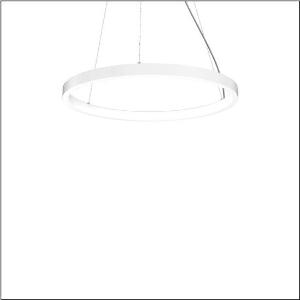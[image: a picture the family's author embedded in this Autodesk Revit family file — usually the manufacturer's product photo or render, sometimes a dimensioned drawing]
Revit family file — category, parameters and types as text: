
# Revit family: silica_r__21_ring-i_5pjbi3d1004a_d7a1
name_source: partatom
category: Lighting Fixtures
units: mm (PartAtom-declared; Revit-internal decimal feet)

## family parameters
Cut with Voids When Loaded = No
Host = Face
Light Source = No
Part Type = Normal
Room Calculation Point = No
Round Connector Dimension = Use Diameter
Shared = No

## types (1)
- Silica® 21 Ring-I (1 x LED, 6120 lm, 105 W, 3000K)
    Apparent Load = 105 VA
    CIE Flux Codes = 22 48 76 50 101
    Color Rendering = 80
    Color Temperature = 3000K
    Default Elevation = 1800 mm
    Description = Silica® 21 Ring-I, suspended luminaire, of PMMA, frosted, light emission: inner ring side luminous distribution, primary light characteristic: symmetric, installation type: suspended mounting, LED, rated luminous flux: 6.120lm, luminous efficacy: 58lm/W, light colour: 830, colour temperature: 3000K, with terminal, 5-pole, mains connection: 230V, AC/DC, 0/50..60Hz, rated input power: 105W, housing, of extruded aluminium section, traffic white (RAL 9016), diameter: 1.090mm, ceiling canopy, traffic white (RAL 9016), protection rating (lamp compartment): IP40, insulation class (complete): insulation class I (protective earthing), certification: CE, impact resistance: IK02, permissible operating ambient temperature: 0..+35°C, packaging unit: 1 piece
    Height = 48 mm  [stored 0.15748 ft]
    Lamp = 1 x LED
    Lamp Light Flux = 6120 lm
    Lamp Power = 105 W
    Lamp count = 1
    Length = 1090 mm
    Luminous efficacy = 58 lm/W
    Manufacturer = Siteco
    ModVariant = No
    Model = 5PJBI3D1004A
    Mounting Place = Ceiling
    Mounting Type = Pendant
    Number of Poles = 1
    OnlyDefault = Yes
    Power Factor = 1
    Product Name = Silica® 21 Ring-I
    Product group = suspended luminaire
    ProductGroupID = 904
    Protection Class = Protection class I
    Protection Degree = IP 40
    RLX_Detail_Level = 1
    RLX_Emergency_Light_Flux = 0 lm
    RLX_Emergency_Type = 0
    RLX_Emergency_Type_DB = No
    RlxData = <blob elided: 12785 chars, md5=375fb4e9>
    Socket = socket
    Standby Power = 0 W
    System Light Flux = 6120 lm
    System Power = 105 W
    Type Comments = Product without accessories
    Type Image = l_1258371.jpg
    URL = http://relux.com
    VarID = ---
    Voltage = 0 V
    Weight = 0.00 kg
    Width = 0 mm  [stored 0 ft]

note: [stored X ft] marks values corroborated as IEEE doubles in the binary element streams (Revit-internal decimal feet)

## geometry (parser evidence)
native form markers: Sweep x12
no freeform markers — native parametric forms only
